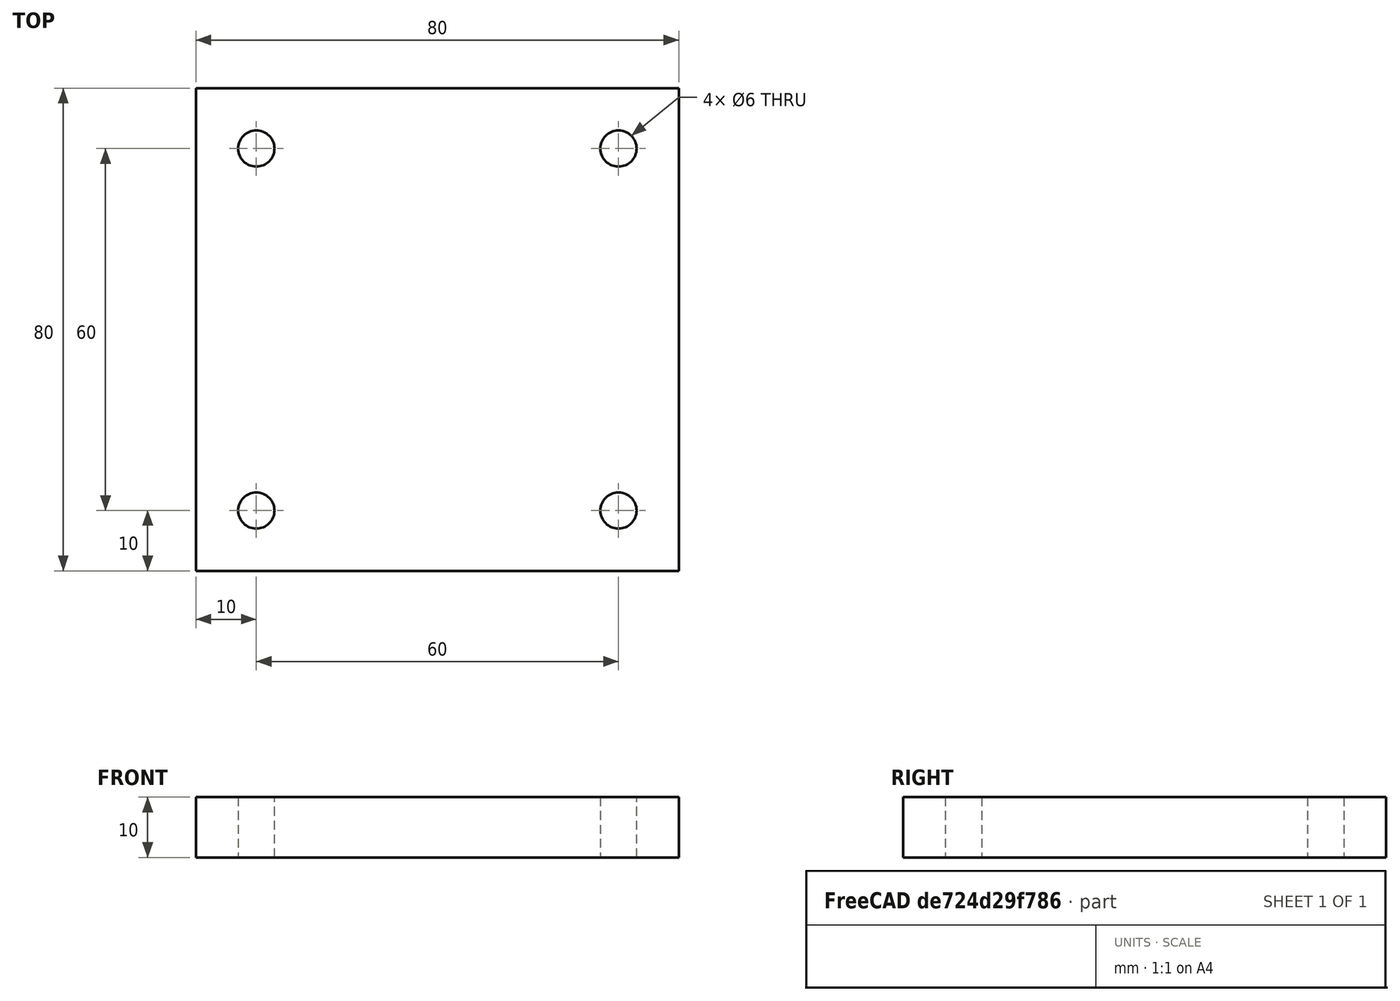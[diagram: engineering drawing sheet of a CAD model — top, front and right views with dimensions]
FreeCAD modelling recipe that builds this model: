
FCSTD DOCUMENT  (FreeCAD 0.18R16093 +53 (Git))
Label: CLAMP_1
License: All rights reserved
LicenseURL: http://en.wikipedia.org/wiki/All_rights_reserved
objects: Sketcher::SketchObject×1, PartDesign::Pad×1, PartDesign::Body×1
note: 4 computed .brp shape members not serialized (recipe doc carries the construction recipe); baked Part::Feature solids carry a one-line shape summary decoded from their .brp

FEATURE [Sketcher::SketchObject] Sketch
  MapMode = 5
  Support = -> [XY_Plane]
  sketch-geometry (9):
    g0: LineSegment StartX=-40 StartY=40 StartZ=0 EndX=-40 EndY=-40 EndZ=0
    g1: LineSegment StartX=-40 StartY=-40 StartZ=0 EndX=40 EndY=-40 EndZ=0
    g2: LineSegment StartX=40 StartY=-40 StartZ=0 EndX=40 EndY=40 EndZ=0
    g3: LineSegment StartX=40 StartY=40 StartZ=0 EndX=-40 EndY=40 EndZ=0
    g4: Circle [constr] CenterX=0 CenterY=0 CenterZ=0 NormalX=0 NormalY=0 NormalZ=1 AngleXU=0 Radius=56.5685
    g5: Circle CenterX=-30 CenterY=30 CenterZ=0 NormalX=0 NormalY=0 NormalZ=1 AngleXU=0 Radius=3
    g6: Circle CenterX=30 CenterY=30 CenterZ=0 NormalX=0 NormalY=0 NormalZ=1 AngleXU=0 Radius=3
    g7: Circle CenterX=-30 CenterY=-30 CenterZ=0 NormalX=0 NormalY=0 NormalZ=1 AngleXU=0 Radius=3
    g8: Circle CenterX=30 CenterY=-30 CenterZ=0 NormalX=0 NormalY=0 NormalZ=1 AngleXU=0 Radius=3
  constraints (26):
    c: Coincident(g0,g1)
    c: Coincident(g1,g2)
    c: Coincident(g2,g3)
    c: Coincident(g3,g0)
    c: Equal(g0,g1)
    c: Equal(g0,g2)
    c: Equal(g0,g3)
    c: PointOnObject(g0,g4)
    c: PointOnObject(g1,g4)
    c: PointOnObject(g2,g4)
    c: PointOnObject(g3,g4)
    c: Coincident(g4,g-1)
    c: Horizontal(g3)
    c: DistanceY(g0,g0) = 80
    c: Radius(g5) = 3
    c: Equal(g5,g6)
    c: Equal(g6,g7)
    c: Equal(g7,g8)
    c: Horizontal(g5,g6)
    c: Horizontal(g7,g8)
    c: Vertical(g7,g5)
    c: Vertical(g6,g8)
    c: DistanceX(g0,g5) = 10
    c: DistanceY(g5,g0) = 10
    c: DistanceX(g6,g2) = 10
    c: DistanceY(g0,g7) = 10
FEATURE [PartDesign::Pad] Pad
  Length = 10
  Length2 = 100
  Profile = -> Sketch
  Type = 0
FEATURE [PartDesign::Body] Body
  Group = -> [Sketch,Pad]
  Origin = -> Origin
  Tip = -> Pad
